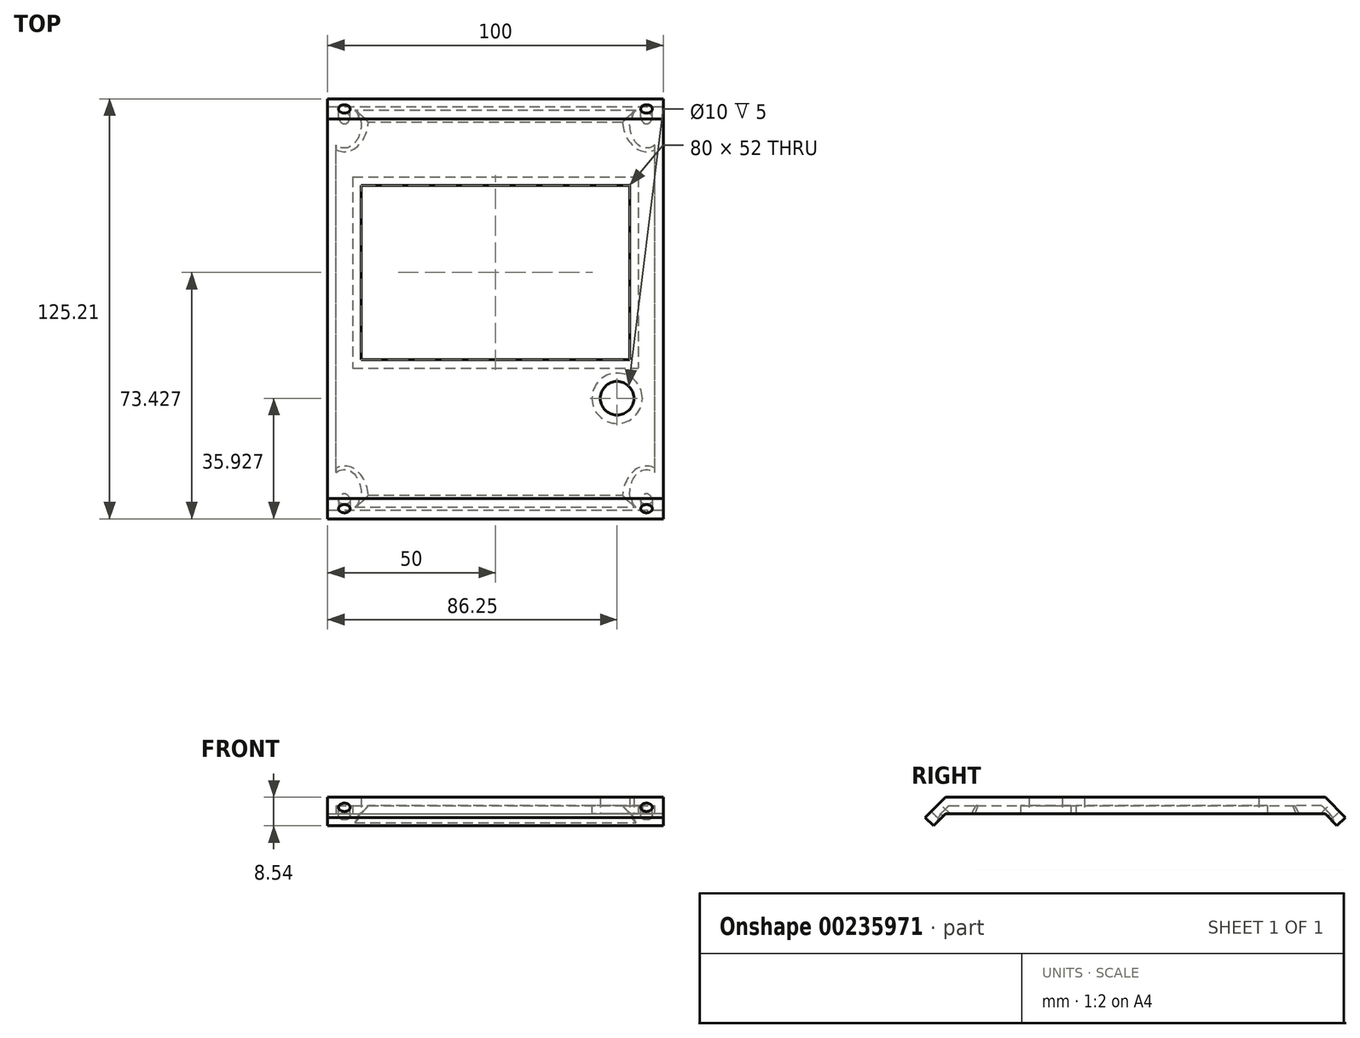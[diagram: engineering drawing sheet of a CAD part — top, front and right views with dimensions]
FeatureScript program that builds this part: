
annotation { "Feature Type Name" : "Feature", "Feature Type Description" : "" }
export const myFeature = defineFeature(function(context is Context, id is Id, definition is map)
    precondition{}
    {
        {
            var Q0;
            Q0=qCreatedBy(makeId("Top.planeOp"),FACE);
            var sketch = newSketch(context, id + "F0", { "sketchPlane" : qUnion([Q0])});
            skLineSegment(sketch, "E0", {"start": v(0, 0) * mm, "end": v(0, 113.14) * mm});
            skLineSegment(sketch, "E1.0", {"start": v(100, 0) * mm, "end": v(100, 113.14) * mm});
            skLineSegment(sketch, "E2", {"start": v(100, 113.14) * mm, "end": v(0, 113.14) * mm});
            skLineSegment(sketch, "E3", {"start": v(0, 0) * mm, "end": v(100, 0) * mm});
            skLineSegment(sketch, "E4.0", {"start": v(10, 93.39) * mm, "end": v(90, 93.39) * mm});
            skLineSegment(sketch, "E5.0", {"start": v(10, 93.39) * mm, "end": v(10, 41.39) * mm});
            skLineSegment(sketch, "E6.0", {"start": v(90, 93.39) * mm, "end": v(90, 41.39) * mm});
            skCircle(sketch, "E7.0", {"center": v(86.25, 29.89) * mm, "radius": 5 * mm});
            skLineSegment(sketch, "E8", {"start": v(10, 41.39) * mm, "end": v(90, 41.39) * mm});
            skSolve(sketch);
        }
        {
            var Q0;
            Q0=qSketchRegion(id+"F0",true);
            extrude(context, id + "F1", {"entities" : qUnion([Q0]), "depth" : 5 * mm});
        }
        {
            var Q0;
            Q0=makeQuery(id+"F1.opExtrude","SWEPT_FACE",FACE,{"disambiguationData":[OSD([sQuery(id+"F0.wireOp",EDGE,"E0")])]});
            var sketch = newSketch(context, id + "F2", { "sketchPlane" : qUnion([Q0])});
            skLineSegment(sketch, "E9", {"start": v(0, 0) * mm, "end": v(3.54, -3.54) * mm});
            skLineSegment(sketch, "E10", {"start": v(3.54, -3.54) * mm, "end": v(6.04, -1.04) * mm});
            skLineSegment(sketch, "E11", {"start": v(6.04, -1.04) * mm, "end": v(0, 5) * mm});
            skLineSegment(sketch, "E12", {"start": v(-113.14, 0) * mm, "end": v(-116.67, -3.54) * mm});
            skLineSegment(sketch, "E13", {"start": v(-116.67, -3.54) * mm, "end": v(-119.17, -1.04) * mm});
            skLineSegment(sketch, "E14", {"start": v(-119.17, -1.04) * mm, "end": v(-113.14, 5) * mm});
            skLineSegment(sketch, "E15", {"start": v(-113.14, 0) * mm, "end": v(-113.14, 5) * mm});
            skLineSegment(sketch, "E16", {"start": v(0, 0) * mm, "end": v(0, 5) * mm});
            skSolve(sketch);
        }
        {
            var Q0;
            Q0=qSketchRegion(id+"F2",true);
            var Q1;
            Q1=makeQuery(id+"F1.opExtrude","SWEPT_FACE",FACE,{"disambiguationData":[OSD([sQuery(id+"F0.wireOp",EDGE,"E1.0")])]});
            extrude(context, id + "F3", {"entities" : qUnion([Q0]), "operationType" : NewBodyOperationType.ADD, "endBound" : BoundingType.UP_TO_SURFACE, "oppositeDirection" : true, "endBoundEntityFace" : qUnion([Q1]), "depth" : 25 * mm});
        }
        {
            var Q0;
            Q0=makeQuery(id+"F3.opExtrude","SWEPT_FACE",FACE,{"disambiguationData":[OSD([sQuery(id+"F2.wireOp",EDGE,"E14")])]});
            var sketch = newSketch(context, id + "F4", { "sketchPlane" : qUnion([Q0])});
            skCircle(sketch, "E17", {"center": v(-5, -80.73) * mm, "radius": 1.75 * mm});
            skPoint(sketch, "E17.centerSnap0", {"position": v(0, -80.73) * mm});
            skCircle(sketch, "E18", {"center": v(-95, -80.73) * mm, "radius": 1.75 * mm});
            skSolve(sketch);
        }
        {
            var Q0;
            Q0=qSketchRegion(id+"F4",true);
            extrude(context, id + "F5", {"entities" : qUnion([Q0]), "operationType" : NewBodyOperationType.REMOVE, "endBound" : BoundingType.THROUGH_ALL, "oppositeDirection" : true, "depth" : 25 * mm});
        }
        {
            var Q0;
            Q0=makeQuery(id+"F3.opExtrude","SWEPT_FACE",FACE,{"disambiguationData":[OSD([sQuery(id+"F2.wireOp",EDGE,"E11")])]});
            var sketch = newSketch(context, id + "F6", { "sketchPlane" : qUnion([Q0])});
            skCircle(sketch, "E19", {"center": v(95, -0.73) * mm, "radius": 1.75 * mm});
            skPoint(sketch, "E19.centerSnap0", {"position": v(100, -0.73) * mm});
            skCircle(sketch, "E20", {"center": v(5, -0.73) * mm, "radius": 1.75 * mm});
            skSolve(sketch);
        }
        {
            var Q0;
            Q0=qSketchRegion(id+"F6",true);
            extrude(context, id + "F7", {"entities" : qUnion([Q0]), "operationType" : NewBodyOperationType.REMOVE, "endBound" : BoundingType.THROUGH_ALL, "oppositeDirection" : true, "depth" : 25 * mm});
        }
        {
            var Q0;
            Q0=makeQuery(id+"F1.opExtrude","CAP_FACE",FACE,{"disambiguationData":[OSD([sQuery(id+"F0.wireOp",EDGE,"E0"),sQuery(id+"F0.wireOp",EDGE,"E2"),sQuery(id+"F0.wireOp",EDGE,"E1.0"),sQuery(id+"F0.wireOp",EDGE,"E3"),sQuery(id+"F0.wireOp",EDGE,"E4.0"),sQuery(id+"F0.wireOp",EDGE,"E5.0"),sQuery(id+"F0.wireOp",EDGE,"671c34b5-c660-4aef-a58d-1520eb65294c.0"),sQuery(id+"F0.wireOp",EDGE,"E6.0"),sQuery(id+"F0.wireOp",EDGE,"E7.0")])],"isStart":true});
            shell(context, id + "F8", {"entities" : qUnion([Q0]), "thickness" : 2.5 * mm});
        }
        {
            var Q0;
            Q0=makeQuery(id+"F8.opShell","OFFSET_EDGE",EDGE,{"disambiguationData":[OSD([sQuery(id+"F0.wireOp",EDGE,"E0"),sQuery(id+"F0.wireOp",EDGE,"E2"),sQuery(id+"F2.wireOp",EDGE,"E12"),sQuery(id+"F2.wireOp",EDGE,"E15")]),OD(1.0)]});
            var Q1;
            Q1=makeQuery(id+"F8.opShell","OFFSET_EDGE",EDGE,{"disambiguationData":[OSD([sQuery(id+"F0.wireOp",EDGE,"E0"),sQuery(id+"F0.wireOp",EDGE,"E3"),sQuery(id+"F2.wireOp",EDGE,"E9"),sQuery(id+"F2.wireOp",EDGE,"E16")]),OD(1.0)]});
            chamfer(context, id + "F9", {"entities" : qUnion([Q0, Q1]), "width" : 1.5 * mm, "tangentPropagation" : true});
        }
        {
            var Q0;
            Q0=makeQuery(id+"F9.opChamfer","BLEND_EDGE",EDGE,{"blendedFrom":[makeQuery(id+"F8.opShell","OFFSET_EDGE",EDGE,{"disambiguationData":[OSD([sQuery(id+"F0.wireOp",EDGE,"E0"),sQuery(id+"F0.wireOp",EDGE,"E3"),sQuery(id+"F2.wireOp",EDGE,"E9"),sQuery(id+"F2.wireOp",EDGE,"E16")]),OD(1.0)]}),makeQuery(id+"F8.opShell","OFFSET_FACE",FACE,{"disambiguationData":[OSD([sQuery(id+"F2.wireOp",EDGE,"E11")])]})],"blendedInto":[makeQuery(id+"F8.opShell","OFFSET_FACE",FACE,{"disambiguationData":[OSD([sQuery(id+"F2.wireOp",EDGE,"E11")])]})]});
            var Q1;
            Q1=makeQuery(id+"F9.opChamfer","BLEND_EDGE",EDGE,{"blendedFrom":[makeQuery(id+"F8.opShell","OFFSET_EDGE",EDGE,{"disambiguationData":[OSD([sQuery(id+"F0.wireOp",EDGE,"E0"),sQuery(id+"F0.wireOp",EDGE,"E2"),sQuery(id+"F2.wireOp",EDGE,"E12"),sQuery(id+"F2.wireOp",EDGE,"E15")]),OD(1.0)]}),makeQuery(id+"F8.opShell","OFFSET_FACE",FACE,{"disambiguationData":[OSD([sQuery(id+"F2.wireOp",EDGE,"E14")])]})],"blendedInto":[makeQuery(id+"F8.opShell","OFFSET_FACE",FACE,{"disambiguationData":[OSD([sQuery(id+"F2.wireOp",EDGE,"E14")])]})]});
            fillet(context, id + "F10", {"entities" : qUnion([Q0, Q1]), "radius" : 5 * mm, "tangentPropagation" : true, "allowEdgeOverflow" : false});
        }
        {
            var Q0;
            Q0=makeQuery(id+"F8.opShell","TWEAK_EDGE",EDGE,{"derivedFrom":[makeQuery(id+"F1.opExtrude","CAP_FACE",FACE,{"disambiguationData":[OSD([sQuery(id+"F0.wireOp",EDGE,"E0"),sQuery(id+"F0.wireOp",EDGE,"E2"),sQuery(id+"F0.wireOp",EDGE,"E1.0"),sQuery(id+"F0.wireOp",EDGE,"E3"),sQuery(id+"F0.wireOp",EDGE,"E4.0"),sQuery(id+"F0.wireOp",EDGE,"E5.0"),sQuery(id+"F0.wireOp",EDGE,"E6.0"),sQuery(id+"F0.wireOp",EDGE,"E7.0"),sQuery(id+"F0.wireOp",EDGE,"E8")])],"isStart":false}),makeQuery(id+"F5.boolean.opBoolean","COPY",FACE,{"derivedFrom":makeQuery(id+"F5.opExtrude","SWEPT_FACE",FACE,{"disambiguationData":[OSD([sQuery(id+"F4.wireOp",EDGE,"E18")])]})})]});
            var Q1;
            Q1=makeQuery(id+"F8.opShell","TWEAK_EDGE",EDGE,{"derivedFrom":[makeQuery(id+"F1.opExtrude","CAP_FACE",FACE,{"disambiguationData":[OSD([sQuery(id+"F0.wireOp",EDGE,"E0"),sQuery(id+"F0.wireOp",EDGE,"E2"),sQuery(id+"F0.wireOp",EDGE,"E1.0"),sQuery(id+"F0.wireOp",EDGE,"E3"),sQuery(id+"F0.wireOp",EDGE,"E4.0"),sQuery(id+"F0.wireOp",EDGE,"E5.0"),sQuery(id+"F0.wireOp",EDGE,"E6.0"),sQuery(id+"F0.wireOp",EDGE,"E7.0"),sQuery(id+"F0.wireOp",EDGE,"E8")])],"isStart":false}),makeQuery(id+"F7.boolean.opBoolean","COPY",FACE,{"derivedFrom":makeQuery(id+"F7.opExtrude","SWEPT_FACE",FACE,{"disambiguationData":[OSD([sQuery(id+"F6.wireOp",EDGE,"E19")])]})})]});
            var Q2;
            Q2=makeQuery(id+"F8.opShell","TWEAK_EDGE",EDGE,{"derivedFrom":[makeQuery(id+"F1.opExtrude","CAP_FACE",FACE,{"disambiguationData":[OSD([sQuery(id+"F0.wireOp",EDGE,"E0"),sQuery(id+"F0.wireOp",EDGE,"E2"),sQuery(id+"F0.wireOp",EDGE,"E1.0"),sQuery(id+"F0.wireOp",EDGE,"E3"),sQuery(id+"F0.wireOp",EDGE,"E4.0"),sQuery(id+"F0.wireOp",EDGE,"E5.0"),sQuery(id+"F0.wireOp",EDGE,"E6.0"),sQuery(id+"F0.wireOp",EDGE,"E7.0"),sQuery(id+"F0.wireOp",EDGE,"E8")])],"isStart":false}),makeQuery(id+"F7.boolean.opBoolean","COPY",FACE,{"derivedFrom":makeQuery(id+"F7.opExtrude","SWEPT_FACE",FACE,{"disambiguationData":[OSD([sQuery(id+"F6.wireOp",EDGE,"E20")])]})})]});
            var Q3;
            Q3=makeQuery(id+"F8.opShell","TWEAK_EDGE",EDGE,{"derivedFrom":[makeQuery(id+"F1.opExtrude","CAP_FACE",FACE,{"disambiguationData":[OSD([sQuery(id+"F0.wireOp",EDGE,"E0"),sQuery(id+"F0.wireOp",EDGE,"E2"),sQuery(id+"F0.wireOp",EDGE,"E1.0"),sQuery(id+"F0.wireOp",EDGE,"E3"),sQuery(id+"F0.wireOp",EDGE,"E4.0"),sQuery(id+"F0.wireOp",EDGE,"E5.0"),sQuery(id+"F0.wireOp",EDGE,"E6.0"),sQuery(id+"F0.wireOp",EDGE,"E7.0"),sQuery(id+"F0.wireOp",EDGE,"E8")])],"isStart":false}),makeQuery(id+"F5.boolean.opBoolean","COPY",FACE,{"derivedFrom":makeQuery(id+"F5.opExtrude","SWEPT_FACE",FACE,{"disambiguationData":[OSD([sQuery(id+"F4.wireOp",EDGE,"E17")])]})})]});
            chamfer(context, id + "F11", {"entities" : qUnion([Q0, Q1, Q2, Q3]), "width" : 3 * mm, "tangentPropagation" : true});
        }
    });
